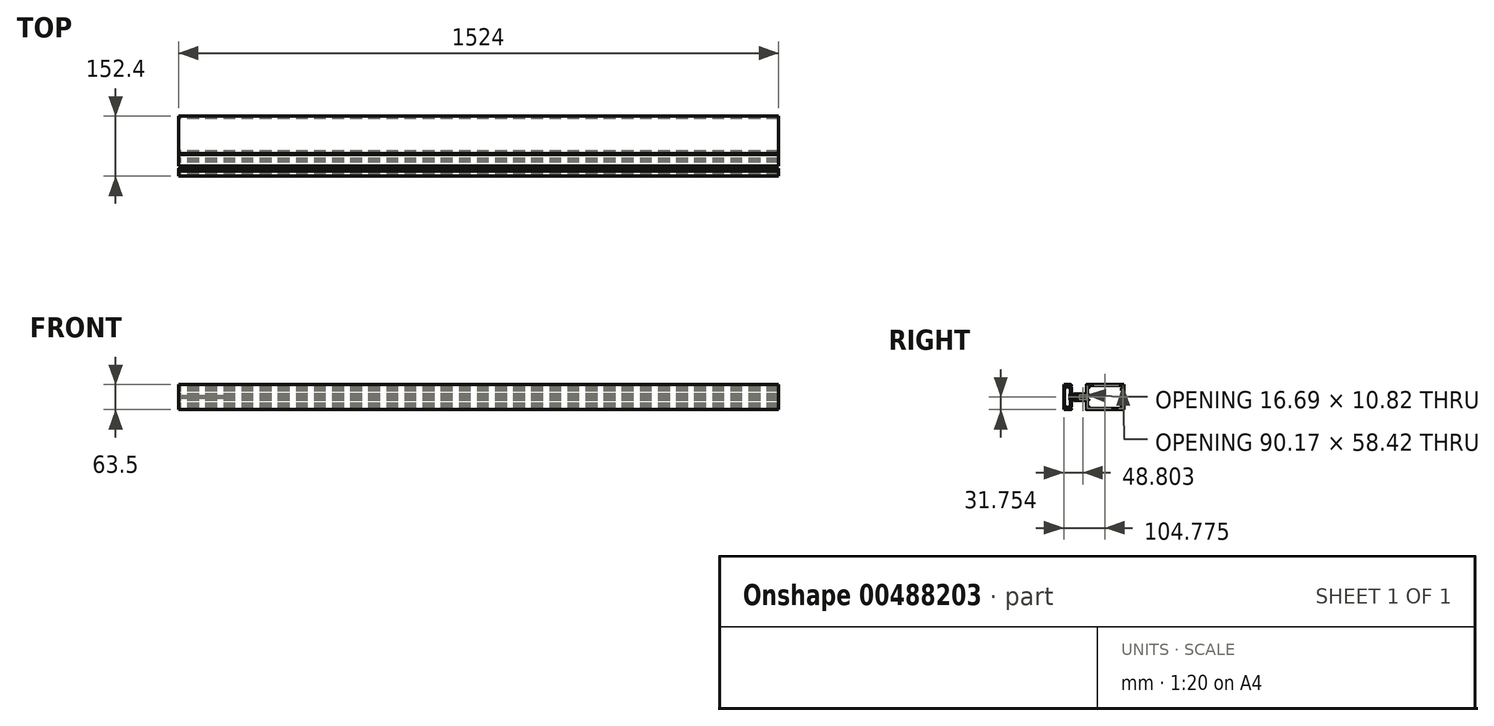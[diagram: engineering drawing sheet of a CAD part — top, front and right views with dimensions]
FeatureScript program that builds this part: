
annotation { "Feature Type Name" : "Feature", "Feature Type Description" : "" }
export const myFeature = defineFeature(function(context is Context, id is Id, definition is map)
    precondition{}
    {
        {
            var Q0;
            Q0=qCreatedBy(makeId("Right.planeOp"),FACE);
            var sketch = newSketch(context, id + "F0", { "sketchPlane" : qUnion([Q0])});
            skLineSegment(sketch, "E0", {"start": v(76.2, -31.75) * mm, "end": v(76.2, -31.26) * mm});
            skLineSegment(sketch, "E1", {"start": v(-25.4, -19.05) * mm, "end": v(-50.8, -19.05) * mm});
            skLineSegment(sketch, "E2", {"start": v(-25.4, 19.05) * mm, "end": v(-50.8, 19.05) * mm});
            skLineSegment(sketch, "E3", {"start": v(-23.22, 5.41) * mm, "end": v(-34.99, 5.41) * mm});
            skArc(sketch, "E4", {"start": v(-34.99, 5.41) * mm, "mid": v(-35.74, 4.75) * mm, "end": v(-35.19, 3.92) * mm});
            skLineSegment(sketch, "E5", {"start": v(-35.19, 3.92) * mm, "end": v(-33.68, 3.51) * mm});
            skArc(sketch, "E6", {"start": v(-33.68, 3.51) * mm, "mid": v(-30.99, 0) * mm, "end": v(-33.68, -3.5) * mm});
            skLineSegment(sketch, "E7", {"start": v(-33.68, -3.5) * mm, "end": v(-35.19, -3.9) * mm});
            skArc(sketch, "E8", {"start": v(-35.19, -3.9) * mm, "mid": v(-35.74, -4.74) * mm, "end": v(-34.99, -5.4) * mm});
            skLineSegment(sketch, "E9", {"start": v(-34.99, -5.4) * mm, "end": v(-23.22, -5.4) * mm});
            skArc(sketch, "E10", {"start": v(-23.22, -5.4) * mm, "mid": v(-22.19, -4.3) * mm, "end": v(-20.73, -3.88) * mm});
            skLineSegment(sketch, "E11", {"start": v(-20.73, -3.88) * mm, "end": v(-19.05, -3.88) * mm});
            skLineSegment(sketch, "E12", {"start": v(-19.05, -3.88) * mm, "end": v(-19.05, 3.9) * mm});
            skLineSegment(sketch, "E13", {"start": v(-19.05, 3.9) * mm, "end": v(-20.73, 3.9) * mm});
            skArc(sketch, "E14", {"start": v(-20.73, 3.9) * mm, "mid": v(-22.19, 4.3) * mm, "end": v(-23.22, 5.41) * mm});
            skLineSegment(sketch, "E15", {"start": v(-19.05, 15.5) * mm, "end": v(-19.05, 6.68) * mm});
            skArc(sketch, "E16", {"start": v(-19.05, 6.68) * mm, "mid": v(-19.12, 6.5) * mm, "end": v(-19.3, 6.43) * mm});
            skLineSegment(sketch, "E17", {"start": v(-19.3, 6.43) * mm, "end": v(-20.73, 6.43) * mm});
            skArc(sketch, "E18", {"start": v(-20.73, 6.43) * mm, "mid": v(-20.9, 6.5) * mm, "end": v(-20.98, 6.68) * mm});
            skLineSegment(sketch, "E19", {"start": v(-20.98, 6.68) * mm, "end": v(-20.98, 7.7) * mm});
            skArc(sketch, "E20", {"start": v(-20.98, 7.7) * mm, "mid": v(-21.05, 7.88) * mm, "end": v(-21.23, 7.95) * mm});
            skLineSegment(sketch, "E21", {"start": v(-21.23, 7.95) * mm, "end": v(-50.8, 7.95) * mm});
            skLineSegment(sketch, "E22", {"start": v(-50.8, 7.95) * mm, "end": v(-50.8, 6.94) * mm});
            skLineSegment(sketch, "E23", {"start": v(-50.8, 6.94) * mm, "end": v(-51.18, 6.56) * mm});
            skLineSegment(sketch, "E24", {"start": v(-51.18, 6.56) * mm, "end": v(-50.8, 6.18) * mm});
            skLineSegment(sketch, "E25", {"start": v(-50.8, 6.18) * mm, "end": v(-50.8, 4.32) * mm});
            skLineSegment(sketch, "E26", {"start": v(-50.8, 4.32) * mm, "end": v(-51.18, 3.94) * mm});
            skLineSegment(sketch, "E27", {"start": v(-51.18, 3.94) * mm, "end": v(-50.8, 3.56) * mm});
            skLineSegment(sketch, "E28", {"start": v(-50.8, 3.56) * mm, "end": v(-50.8, 2.54) * mm});
            skLineSegment(sketch, "E29", {"start": v(-50.8, 2.54) * mm, "end": v(-39.88, 2.54) * mm});
            skLineSegment(sketch, "E30", {"start": v(-39.88, 2.54) * mm, "end": v(-34.34, 1.06) * mm});
            skArc(sketch, "E31", {"start": v(-34.34, 1.06) * mm, "mid": v(-33.53, 0) * mm, "end": v(-34.34, -1.05) * mm});
            skLineSegment(sketch, "E32", {"start": v(-34.34, -1.05) * mm, "end": v(-39.88, -2.54) * mm});
            skLineSegment(sketch, "E33", {"start": v(-39.88, -2.54) * mm, "end": v(-50.8, -2.54) * mm});
            skLineSegment(sketch, "E34", {"start": v(-50.8, -2.54) * mm, "end": v(-50.8, -3.55) * mm});
            skLineSegment(sketch, "E35", {"start": v(-50.8, -3.55) * mm, "end": v(-51.18, -3.93) * mm});
            skLineSegment(sketch, "E36", {"start": v(-51.18, -3.93) * mm, "end": v(-50.8, -4.31) * mm});
            skLineSegment(sketch, "E37", {"start": v(-50.8, -4.31) * mm, "end": v(-50.8, -6.17) * mm});
            skLineSegment(sketch, "E38", {"start": v(-50.8, -6.17) * mm, "end": v(-51.18, -6.55) * mm});
            skLineSegment(sketch, "E39", {"start": v(-51.18, -6.55) * mm, "end": v(-50.8, -6.93) * mm});
            skLineSegment(sketch, "E40", {"start": v(-50.8, -6.93) * mm, "end": v(-50.8, -7.95) * mm});
            skLineSegment(sketch, "E41", {"start": v(-50.8, -7.95) * mm, "end": v(-21.23, -7.95) * mm});
            skArc(sketch, "E42", {"start": v(-21.23, -7.95) * mm, "mid": v(-21.05, -7.87) * mm, "end": v(-20.98, -7.7) * mm});
            skLineSegment(sketch, "E43", {"start": v(-20.98, -7.7) * mm, "end": v(-20.98, -6.68) * mm});
            skArc(sketch, "E44", {"start": v(-20.98, -6.68) * mm, "mid": v(-20.9, -6.5) * mm, "end": v(-20.73, -6.42) * mm});
            skLineSegment(sketch, "E45", {"start": v(-20.73, -6.42) * mm, "end": v(-19.3, -6.42) * mm});
            skArc(sketch, "E46", {"start": v(-19.3, -6.42) * mm, "mid": v(-19.12, -6.5) * mm, "end": v(-19.05, -6.68) * mm});
            skLineSegment(sketch, "E47", {"start": v(-19.05, -6.68) * mm, "end": v(-19.05, -15.49) * mm});
            skLineSegment(sketch, "E48", {"start": v(-19.05, -15.49) * mm, "end": v(-18.67, -15.87) * mm});
            skLineSegment(sketch, "E49", {"start": v(-18.67, -15.87) * mm, "end": v(-19.05, -16.25) * mm});
            skLineSegment(sketch, "E50", {"start": v(-19.05, -16.25) * mm, "end": v(-19.05, -25.2) * mm});
            skArc(sketch, "E51", {"start": v(-19.05, -25.2) * mm, "mid": v(-18.81, -25.54) * mm, "end": v(-18.4, -25.46) * mm});
            skArc(sketch, "E52", {"start": v(-18.4, -25.46) * mm, "mid": v(-17.66, -24.96) * mm, "end": v(-16.78, -24.79) * mm});
            skLineSegment(sketch, "E53", {"start": v(-16.78, -24.79) * mm, "end": v(-16.51, -24.79) * mm});
            skArc(sketch, "E54", {"start": v(-16.51, -24.79) * mm, "mid": v(-15.61, -25.16) * mm, "end": v(-15.24, -26.06) * mm});
            skLineSegment(sketch, "E55", {"start": v(-15.24, -26.06) * mm, "end": v(-15.24, -28.3) * mm});
            skArc(sketch, "E56", {"start": v(-15.24, -28.3) * mm, "mid": v(-15.61, -29.19) * mm, "end": v(-16.51, -29.56) * mm});
            skLineSegment(sketch, "E57", {"start": v(-16.51, -29.56) * mm, "end": v(-16.78, -29.56) * mm});
            skArc(sketch, "E58", {"start": v(-16.78, -29.56) * mm, "mid": v(-17.66, -29.39) * mm, "end": v(-18.4, -28.89) * mm});
            skArc(sketch, "E59", {"start": v(-18.4, -28.89) * mm, "mid": v(-18.81, -28.8) * mm, "end": v(-19.05, -29.16) * mm});
            skLineSegment(sketch, "E60", {"start": v(-19.05, -29.16) * mm, "end": v(-19.05, -31.24) * mm});
            skArc(sketch, "E61", {"start": v(-19.05, -31.24) * mm, "mid": v(-18.9, -31.6) * mm, "end": v(-18.54, -31.75) * mm});
            skLineSegment(sketch, "E62", {"start": v(-18.54, -31.75) * mm, "end": v(76.2, -31.75) * mm});
            skLineSegment(sketch, "E63", {"start": v(76.2, -31.75) * mm, "end": v(76.2, 31.75) * mm});
            skLineSegment(sketch, "E64", {"start": v(76.2, 31.75) * mm, "end": v(-18.54, 31.75) * mm});
            skArc(sketch, "E65", {"start": v(-18.54, 31.75) * mm, "mid": v(-18.9, 31.6) * mm, "end": v(-19.05, 31.25) * mm});
            skLineSegment(sketch, "E66", {"start": v(-19.05, 31.25) * mm, "end": v(-19.05, 29.16) * mm});
            skArc(sketch, "E67", {"start": v(-19.05, 29.16) * mm, "mid": v(-18.81, 28.81) * mm, "end": v(-18.4, 28.9) * mm});
            skArc(sketch, "E68", {"start": v(-18.4, 28.9) * mm, "mid": v(-17.66, 29.4) * mm, "end": v(-16.78, 29.57) * mm});
            skLineSegment(sketch, "E69", {"start": v(-16.78, 29.57) * mm, "end": v(-16.51, 29.57) * mm});
            skArc(sketch, "E70", {"start": v(-16.51, 29.57) * mm, "mid": v(-15.61, 29.2) * mm, "end": v(-15.24, 28.3) * mm});
            skLineSegment(sketch, "E71", {"start": v(-15.24, 28.3) * mm, "end": v(-15.24, 26.06) * mm});
            skArc(sketch, "E72", {"start": v(-15.24, 26.06) * mm, "mid": v(-15.61, 25.17) * mm, "end": v(-16.51, 24.8) * mm});
            skLineSegment(sketch, "E73", {"start": v(-16.51, 24.8) * mm, "end": v(-16.78, 24.8) * mm});
            skArc(sketch, "E74", {"start": v(-16.78, 24.8) * mm, "mid": v(-17.66, 24.97) * mm, "end": v(-18.4, 25.47) * mm});
            skArc(sketch, "E75", {"start": v(-18.4, 25.47) * mm, "mid": v(-18.81, 25.55) * mm, "end": v(-19.05, 25.2) * mm});
            skLineSegment(sketch, "E76", {"start": v(-19.05, 25.2) * mm, "end": v(-19.05, 16.26) * mm});
            skLineSegment(sketch, "E77", {"start": v(-19.05, 16.26) * mm, "end": v(-18.67, 15.88) * mm});
            skLineSegment(sketch, "E78", {"start": v(-18.67, 15.88) * mm, "end": v(-19.05, 15.5) * mm});
            skArc(sketch, "E79", {"start": v(-13.2, 5.92) * mm, "mid": v(-12.85, 6.07) * mm, "end": v(-12.7, 6.43) * mm});
            skLineSegment(sketch, "E80", {"start": v(-12.7, 6.43) * mm, "end": v(-12.7, 7.45) * mm});
            skArc(sketch, "E81", {"start": v(-12.7, 7.45) * mm, "mid": v(-12.85, 7.8) * mm, "end": v(-13.2, 7.95) * mm});
            skLineSegment(sketch, "E82", {"start": v(-13.2, 7.95) * mm, "end": v(-15.88, 7.95) * mm});
            skLineSegment(sketch, "E83", {"start": v(-15.88, 7.95) * mm, "end": v(-15.88, 22.74) * mm});
            skLineSegment(sketch, "E84", {"start": v(-15.88, 22.74) * mm, "end": v(-13.2, 22.74) * mm});
            skArc(sketch, "E85", {"start": v(-13.2, 22.74) * mm, "mid": v(-12.85, 22.89) * mm, "end": v(-12.7, 23.25) * mm});
            skLineSegment(sketch, "E86", {"start": v(-12.7, 23.25) * mm, "end": v(-12.7, 28.45) * mm});
            skArc(sketch, "E87", {"start": v(-12.7, 28.45) * mm, "mid": v(-12.48, 29) * mm, "end": v(-11.94, 29.21) * mm});
            skLineSegment(sketch, "E88", {"start": v(-11.94, 29.21) * mm, "end": v(73.66, 29.21) * mm});
            skLineSegment(sketch, "E89", {"start": v(73.66, 29.21) * mm, "end": v(73.66, 25.15) * mm});
            skArc(sketch, "E90", {"start": v(73.66, 25.15) * mm, "mid": v(73.21, 24.07) * mm, "end": v(72.14, 23.63) * mm});
            skLineSegment(sketch, "E91", {"start": v(72.14, 23.63) * mm, "end": v(70.61, 23.63) * mm});
            skLineSegment(sketch, "E92", {"start": v(70.61, 23.63) * mm, "end": v(70.61, 17.66) * mm});
            skLineSegment(sketch, "E93", {"start": v(70.61, 17.66) * mm, "end": v(72.14, 17.66) * mm});
            skArc(sketch, "E94", {"start": v(72.14, 17.66) * mm, "mid": v(73.21, 17.21) * mm, "end": v(73.66, 16.13) * mm});
            skLineSegment(sketch, "E95", {"start": v(73.66, 16.13) * mm, "end": v(73.66, -16.12) * mm});
            skArc(sketch, "E96", {"start": v(73.66, -16.12) * mm, "mid": v(73.21, -17.2) * mm, "end": v(72.14, -17.65) * mm});
            skLineSegment(sketch, "E97", {"start": v(72.14, -17.65) * mm, "end": v(70.61, -17.65) * mm});
            skLineSegment(sketch, "E98", {"start": v(70.61, -17.65) * mm, "end": v(70.61, -23.62) * mm});
            skLineSegment(sketch, "E99", {"start": v(70.61, -23.62) * mm, "end": v(72.14, -23.62) * mm});
            skArc(sketch, "E100", {"start": v(72.14, -23.62) * mm, "mid": v(73.21, -24.06) * mm, "end": v(73.66, -25.14) * mm});
            skLineSegment(sketch, "E101", {"start": v(73.66, -25.14) * mm, "end": v(73.66, -29.2) * mm});
            skLineSegment(sketch, "E102", {"start": v(73.66, -29.2) * mm, "end": v(-11.94, -29.2) * mm});
            skArc(sketch, "E103", {"start": v(-11.94, -29.2) * mm, "mid": v(-12.48, -28.98) * mm, "end": v(-12.7, -28.44) * mm});
            skLineSegment(sketch, "E104", {"start": v(-12.7, -28.44) * mm, "end": v(-12.7, -23.24) * mm});
            skArc(sketch, "E105", {"start": v(-12.7, -23.24) * mm, "mid": v(-12.85, -22.88) * mm, "end": v(-13.2, -22.73) * mm});
            skLineSegment(sketch, "E106", {"start": v(-13.2, -22.73) * mm, "end": v(-15.88, -22.73) * mm});
            skLineSegment(sketch, "E107", {"start": v(-15.88, -22.73) * mm, "end": v(-15.88, -7.95) * mm});
            skLineSegment(sketch, "E108", {"start": v(-15.88, -7.95) * mm, "end": v(-13.2, -7.95) * mm});
            skArc(sketch, "E109", {"start": v(-13.2, -7.95) * mm, "mid": v(-12.85, -7.8) * mm, "end": v(-12.7, -7.44) * mm});
            skLineSegment(sketch, "E110", {"start": v(-12.7, -7.44) * mm, "end": v(-12.7, -6.42) * mm});
            skArc(sketch, "E111", {"start": v(-12.7, -6.42) * mm, "mid": v(-12.85, -6.06) * mm, "end": v(-13.2, -5.91) * mm});
            skLineSegment(sketch, "E112", {"start": v(-13.2, -5.91) * mm, "end": v(-16.51, -5.91) * mm});
            skLineSegment(sketch, "E113", {"start": v(-16.51, -5.91) * mm, "end": v(-16.51, 5.92) * mm});
            skLineSegment(sketch, "E114", {"start": v(-16.51, 5.92) * mm, "end": v(-13.2, 5.92) * mm});
            skLineSegment(sketch, "E115", {"start": v(-19.06, 19.57) * mm, "end": v(-25.4, 19.57) * mm});
            skLineSegment(sketch, "E116", {"start": v(-11.7, 31.76) * mm, "end": v(-14.63, 31.76) * mm});
            skLineSegment(sketch, "E117", {"start": v(-31.75, 11.13) * mm, "end": v(-41.28, 11.13) * mm});
            skLineSegment(sketch, "E118", {"start": v(-41.28, 11.13) * mm, "end": v(-41.28, 7.95) * mm});
            skLineSegment(sketch, "E119", {"start": v(-41.28, 7.95) * mm, "end": v(-50.8, 7.95) * mm});
            skLineSegment(sketch, "E120", {"start": v(-50.8, 7.95) * mm, "end": v(-50.8, 15.88) * mm});
            skLineSegment(sketch, "E121", {"start": v(-50.8, 15.88) * mm, "end": v(-52.39, 15.88) * mm});
            skArc(sketch, "E122", {"start": v(-52.39, 19.05) * mm, "mid": v(-53.98, 17.47) * mm, "end": v(-52.39, 15.88) * mm});
            skLineSegment(sketch, "E123", {"start": v(-52.39, 19.05) * mm, "end": v(-20.64, 19.05) * mm});
            skArc(sketch, "E124", {"start": v(-20.64, 15.88) * mm, "mid": v(-19.05, 17.47) * mm, "end": v(-20.64, 19.05) * mm});
            skLineSegment(sketch, "E125", {"start": v(-20.64, 15.88) * mm, "end": v(-22.23, 15.88) * mm});
            skLineSegment(sketch, "E126", {"start": v(-22.23, 15.88) * mm, "end": v(-22.23, 7.95) * mm});
            skLineSegment(sketch, "E127", {"start": v(-22.23, 7.95) * mm, "end": v(-31.75, 7.95) * mm});
            skLineSegment(sketch, "E128", {"start": v(-31.75, 7.95) * mm, "end": v(-31.75, 11.13) * mm});
            skLineSegment(sketch, "E129", {"start": v(-19.05, -21.43) * mm, "end": v(-19.05, -10.3) * mm});
            skLineSegment(sketch, "E130", {"start": v(-60.33, 6.35) * mm, "end": v(-60.33, -6.35) * mm});
            skLineSegment(sketch, "E131", {"start": v(-74.68, 30.48) * mm, "end": v(-65.43, 30.48) * mm});
            skLineSegment(sketch, "E132", {"start": v(-65.43, 30.48) * mm, "end": v(-65.43, 29.72) * mm});
            skArc(sketch, "E133", {"start": v(-65.43, 29.72) * mm, "mid": v(-64.41, 28.7) * mm, "end": v(-63.4, 29.72) * mm});
            skLineSegment(sketch, "E134", {"start": v(-63.4, 29.72) * mm, "end": v(-63.4, 30.23) * mm});
            skArc(sketch, "E135", {"start": v(-63.4, 30.23) * mm, "mid": v(-63.84, 31.3) * mm, "end": v(-64.92, 31.75) * mm});
            skLineSegment(sketch, "E136", {"start": v(-64.92, 31.75) * mm, "end": v(-76.2, 31.75) * mm});
            skLineSegment(sketch, "E137", {"start": v(-76.2, 31.75) * mm, "end": v(-76.2, -31.75) * mm});
            skLineSegment(sketch, "E138", {"start": v(-76.2, -31.75) * mm, "end": v(-64.92, -31.75) * mm});
            skArc(sketch, "E139", {"start": v(-64.92, -31.75) * mm, "mid": v(-63.84, -31.3) * mm, "end": v(-63.4, -30.22) * mm});
            skLineSegment(sketch, "E140", {"start": v(-63.4, -30.22) * mm, "end": v(-63.4, -29.71) * mm});
            skArc(sketch, "E141", {"start": v(-63.4, -29.71) * mm, "mid": v(-64.41, -28.7) * mm, "end": v(-65.43, -29.71) * mm});
            skLineSegment(sketch, "E142", {"start": v(-65.43, -29.71) * mm, "end": v(-65.43, -30.48) * mm});
            skLineSegment(sketch, "E143", {"start": v(-65.43, -30.48) * mm, "end": v(-74.68, -30.48) * mm});
            skLineSegment(sketch, "E144", {"start": v(-74.68, -30.48) * mm, "end": v(-74.68, 30.48) * mm});
            skLineSegment(sketch, "E145", {"start": v(-57.15, -3.37) * mm, "end": v(-60.33, -3.37) * mm});
            skLineSegment(sketch, "E146", {"start": v(-57.15, 3.38) * mm, "end": v(-60.33, 3.38) * mm});
            skLineSegment(sketch, "E147", {"start": v(-19.06, -19.56) * mm, "end": v(-25.4, -19.56) * mm});
            skLineSegment(sketch, "E148", {"start": v(-11.7, -31.76) * mm, "end": v(-14.63, -31.76) * mm});
            skLineSegment(sketch, "E149", {"start": v(-50.8, -7.95) * mm, "end": v(-50.8, -6.36) * mm});
            skLineSegment(sketch, "E150", {"start": v(-57.15, -7.95) * mm, "end": v(-50.8, -7.95) * mm});
            skLineSegment(sketch, "E151", {"start": v(-50.8, 7.95) * mm, "end": v(-57.15, 7.95) * mm});
            skLineSegment(sketch, "E152", {"start": v(-50.8, 6.37) * mm, "end": v(-50.8, 7.95) * mm});
            skLineSegment(sketch, "E153", {"start": v(-57.15, -7.95) * mm, "end": v(-57.15, -6.36) * mm});
            skLineSegment(sketch, "E154", {"start": v(-57.15, 6.37) * mm, "end": v(-57.15, 7.95) * mm});
            skLineSegment(sketch, "E155", {"start": v(-57.14, 19.57) * mm, "end": v(-50.8, 19.57) * mm});
            skLineSegment(sketch, "E156", {"start": v(-64.5, 31.76) * mm, "end": v(-61.57, 31.76) * mm});
            skLineSegment(sketch, "E157", {"start": v(-57.14, -19.56) * mm, "end": v(-50.8, -19.56) * mm});
            skLineSegment(sketch, "E158", {"start": v(-64.5, -31.76) * mm, "end": v(-61.57, -31.76) * mm});
            skLineSegment(sketch, "E159", {"start": v(-63.14, -23.77) * mm, "end": v(-63.14, -26.67) * mm});
            skLineSegment(sketch, "E160", {"start": v(-63.14, -26.67) * mm, "end": v(-66.57, -26.67) * mm});
            skLineSegment(sketch, "E161", {"start": v(-66.57, -26.67) * mm, "end": v(-69.24, -25.12) * mm});
            skArc(sketch, "E162", {"start": v(-69.24, -25.12) * mm, "mid": v(-70.63, -25.5) * mm, "end": v(-70.26, -26.88) * mm});
            skLineSegment(sketch, "E163", {"start": v(-70.26, -26.88) * mm, "end": v(-65.62, -29.56) * mm});
            skArc(sketch, "E164", {"start": v(-65.62, -29.56) * mm, "mid": v(-64.2, -28.71) * mm, "end": v(-63.14, -29.97) * mm});
            skLineSegment(sketch, "E165", {"start": v(-63.14, -29.97) * mm, "end": v(-63.14, -30.98) * mm});
            skArc(sketch, "E166", {"start": v(-63.14, -30.98) * mm, "mid": v(-62.92, -31.52) * mm, "end": v(-62.38, -31.75) * mm});
            skLineSegment(sketch, "E167", {"start": v(-62.38, -31.75) * mm, "end": v(-57.66, -31.75) * mm});
            skArc(sketch, "E168", {"start": v(-57.66, -31.75) * mm, "mid": v(-57.3, -31.6) * mm, "end": v(-57.15, -31.24) * mm});
            skLineSegment(sketch, "E169", {"start": v(-57.15, -31.24) * mm, "end": v(-57.15, -29.16) * mm});
            skArc(sketch, "E170", {"start": v(-57.15, -29.16) * mm, "mid": v(-57.39, -28.8) * mm, "end": v(-57.8, -28.89) * mm});
            skArc(sketch, "E171", {"start": v(-57.8, -28.89) * mm, "mid": v(-58.54, -29.39) * mm, "end": v(-59.42, -29.56) * mm});
            skLineSegment(sketch, "E172", {"start": v(-59.42, -29.56) * mm, "end": v(-59.7, -29.56) * mm});
            skArc(sketch, "E173", {"start": v(-59.7, -29.56) * mm, "mid": v(-60.59, -29.19) * mm, "end": v(-60.96, -28.3) * mm});
            skLineSegment(sketch, "E174", {"start": v(-60.96, -28.3) * mm, "end": v(-60.96, -26.06) * mm});
            skArc(sketch, "E175", {"start": v(-60.96, -26.06) * mm, "mid": v(-60.59, -25.16) * mm, "end": v(-59.7, -24.79) * mm});
            skLineSegment(sketch, "E176", {"start": v(-59.7, -24.79) * mm, "end": v(-59.42, -24.79) * mm});
            skArc(sketch, "E177", {"start": v(-59.42, -24.79) * mm, "mid": v(-58.54, -24.96) * mm, "end": v(-57.8, -25.46) * mm});
            skArc(sketch, "E178", {"start": v(-57.8, -25.46) * mm, "mid": v(-57.39, -25.54) * mm, "end": v(-57.15, -25.2) * mm});
            skLineSegment(sketch, "E179", {"start": v(-57.15, -25.2) * mm, "end": v(-57.15, -5.71) * mm});
            skLineSegment(sketch, "E180", {"start": v(-57.15, -5.71) * mm, "end": v(-56.77, -5.33) * mm});
            skLineSegment(sketch, "E181", {"start": v(-56.77, -5.33) * mm, "end": v(-57.15, -4.95) * mm});
            skLineSegment(sketch, "E182", {"start": v(-57.15, -4.95) * mm, "end": v(-57.15, 4.96) * mm});
            skLineSegment(sketch, "E183", {"start": v(-57.15, 4.96) * mm, "end": v(-56.77, 5.34) * mm});
            skLineSegment(sketch, "E184", {"start": v(-56.77, 5.34) * mm, "end": v(-57.15, 5.72) * mm});
            skLineSegment(sketch, "E185", {"start": v(-57.15, 5.72) * mm, "end": v(-57.15, 25.2) * mm});
            skArc(sketch, "E186", {"start": v(-57.15, 25.2) * mm, "mid": v(-57.39, 25.55) * mm, "end": v(-57.8, 25.47) * mm});
            skArc(sketch, "E187", {"start": v(-57.8, 25.47) * mm, "mid": v(-58.54, 24.97) * mm, "end": v(-59.42, 24.8) * mm});
            skLineSegment(sketch, "E188", {"start": v(-59.42, 24.8) * mm, "end": v(-59.7, 24.8) * mm});
            skArc(sketch, "E189", {"start": v(-59.7, 24.8) * mm, "mid": v(-60.59, 25.17) * mm, "end": v(-60.96, 26.06) * mm});
            skLineSegment(sketch, "E190", {"start": v(-60.96, 26.06) * mm, "end": v(-60.96, 28.3) * mm});
            skArc(sketch, "E191", {"start": v(-60.96, 28.3) * mm, "mid": v(-60.59, 29.2) * mm, "end": v(-59.7, 29.57) * mm});
            skLineSegment(sketch, "E192", {"start": v(-59.7, 29.57) * mm, "end": v(-59.42, 29.57) * mm});
            skArc(sketch, "E193", {"start": v(-59.42, 29.57) * mm, "mid": v(-58.54, 29.4) * mm, "end": v(-57.8, 28.9) * mm});
            skArc(sketch, "E194", {"start": v(-57.8, 28.9) * mm, "mid": v(-57.39, 28.81) * mm, "end": v(-57.15, 29.16) * mm});
            skLineSegment(sketch, "E195", {"start": v(-57.15, 29.16) * mm, "end": v(-57.15, 31.25) * mm});
            skArc(sketch, "E196", {"start": v(-57.15, 31.25) * mm, "mid": v(-57.3, 31.6) * mm, "end": v(-57.66, 31.75) * mm});
            skLineSegment(sketch, "E197", {"start": v(-57.66, 31.75) * mm, "end": v(-62.38, 31.75) * mm});
            skArc(sketch, "E198", {"start": v(-62.38, 31.75) * mm, "mid": v(-62.92, 31.53) * mm, "end": v(-63.14, 31) * mm});
            skLineSegment(sketch, "E199", {"start": v(-63.14, 31) * mm, "end": v(-63.14, 29.98) * mm});
            skArc(sketch, "E200", {"start": v(-63.14, 29.98) * mm, "mid": v(-64.2, 28.72) * mm, "end": v(-65.62, 29.57) * mm});
            skLineSegment(sketch, "E201", {"start": v(-65.62, 29.57) * mm, "end": v(-70.26, 26.9) * mm});
            skArc(sketch, "E202", {"start": v(-70.26, 26.9) * mm, "mid": v(-70.63, 25.5) * mm, "end": v(-69.24, 25.13) * mm});
            skLineSegment(sketch, "E203", {"start": v(-69.24, 25.13) * mm, "end": v(-66.57, 26.67) * mm});
            skLineSegment(sketch, "E204", {"start": v(-66.57, 26.67) * mm, "end": v(-63.14, 26.67) * mm});
            skLineSegment(sketch, "E205", {"start": v(-63.14, 26.67) * mm, "end": v(-63.14, 23.78) * mm});
            skArc(sketch, "E206", {"start": v(-63.14, 23.78) * mm, "mid": v(-62.7, 22.7) * mm, "end": v(-61.62, 22.25) * mm});
            skLineSegment(sketch, "E207", {"start": v(-61.62, 22.25) * mm, "end": v(-59.7, 22.25) * mm});
            skLineSegment(sketch, "E208", {"start": v(-59.7, 22.25) * mm, "end": v(-59.7, 8.26) * mm});
            skLineSegment(sketch, "E209", {"start": v(-59.7, 8.26) * mm, "end": v(-60.33, 7.62) * mm});
            skLineSegment(sketch, "E210", {"start": v(-60.33, 7.62) * mm, "end": v(-60.33, 0.39) * mm});
            skLineSegment(sketch, "E211", {"start": v(-60.33, 0.39) * mm, "end": v(-59.94, 0) * mm});
            skLineSegment(sketch, "E212", {"start": v(-59.94, 0) * mm, "end": v(-60.33, -0.38) * mm});
            skLineSegment(sketch, "E213", {"start": v(-60.33, -0.38) * mm, "end": v(-60.33, -7.62) * mm});
            skLineSegment(sketch, "E214", {"start": v(-60.33, -7.62) * mm, "end": v(-59.7, -8.25) * mm});
            skLineSegment(sketch, "E215", {"start": v(-59.7, -8.25) * mm, "end": v(-59.7, -22.25) * mm});
            skLineSegment(sketch, "E216", {"start": v(-59.7, -22.25) * mm, "end": v(-61.62, -22.25) * mm});
            skArc(sketch, "E217", {"start": v(-61.62, -22.25) * mm, "mid": v(-62.7, -22.7) * mm, "end": v(-63.14, -23.77) * mm});
            skSolve(sketch);
        }
        {
            var Q0;
            Q0=makeQuery(id+"F0.imprint","IMPRINT",FACE,{"disambiguationData":[TD([[makeQuery(id+"F0.imprint","IMPRINT",EDGE,{"derivedFrom":sQuery(id+"F0.wireOp",EDGE,"E3")}),-1.0]])]});
            var Q1;
            {var subQ3=sQuery(id+"F0.wireOp",EDGE,"E146");Q1=makeQuery(id+"F0.imprint","IMPRINT",FACE,{"disambiguationData":[TD([[makeQuery(id+"F0.imprint","IMPRINT",EDGE,{"derivedFrom":subQ3}),-1.0]])]});}
            var Q2;
            Q2=makeQuery(id+"F0.imprint","IMPRINT",FACE,{"disambiguationData":[TD([[makeQuery(id+"F0.imprint","IMPRINT",EDGE,{"derivedFrom":sQuery(id+"F0.wireOp",EDGE,"E131")}),1.0]])]});
            var Q3;
            {var subQ4=sQuery(id+"F0.wireOp",EDGE,"E145");Q3=makeQuery(id+"F0.imprint","IMPRINT",FACE,{"disambiguationData":[TD([[makeQuery(id+"F0.imprint","IMPRINT",EDGE,{"derivedFrom":subQ4}),1.0]])]});}
            extrude(context, id + "F1", {"entities" : qUnion([Q0, Q1, Q2, Q3]), "depth" : 1524 * mm});
        }
        {
            var Q0;
            {var subQ5=sQuery(id+"F0.wireOp",EDGE,"E145");Q0=makeQuery(id+"F0.imprint","IMPRINT",FACE,{"disambiguationData":[TD([[makeQuery(id+"F0.imprint","IMPRINT",EDGE,{"derivedFrom":subQ5}),-1.0]])]});}
            extrude(context, id + "F2", {"entities" : qUnion([Q0]), "depth" : 127 * mm});
        }
    });
